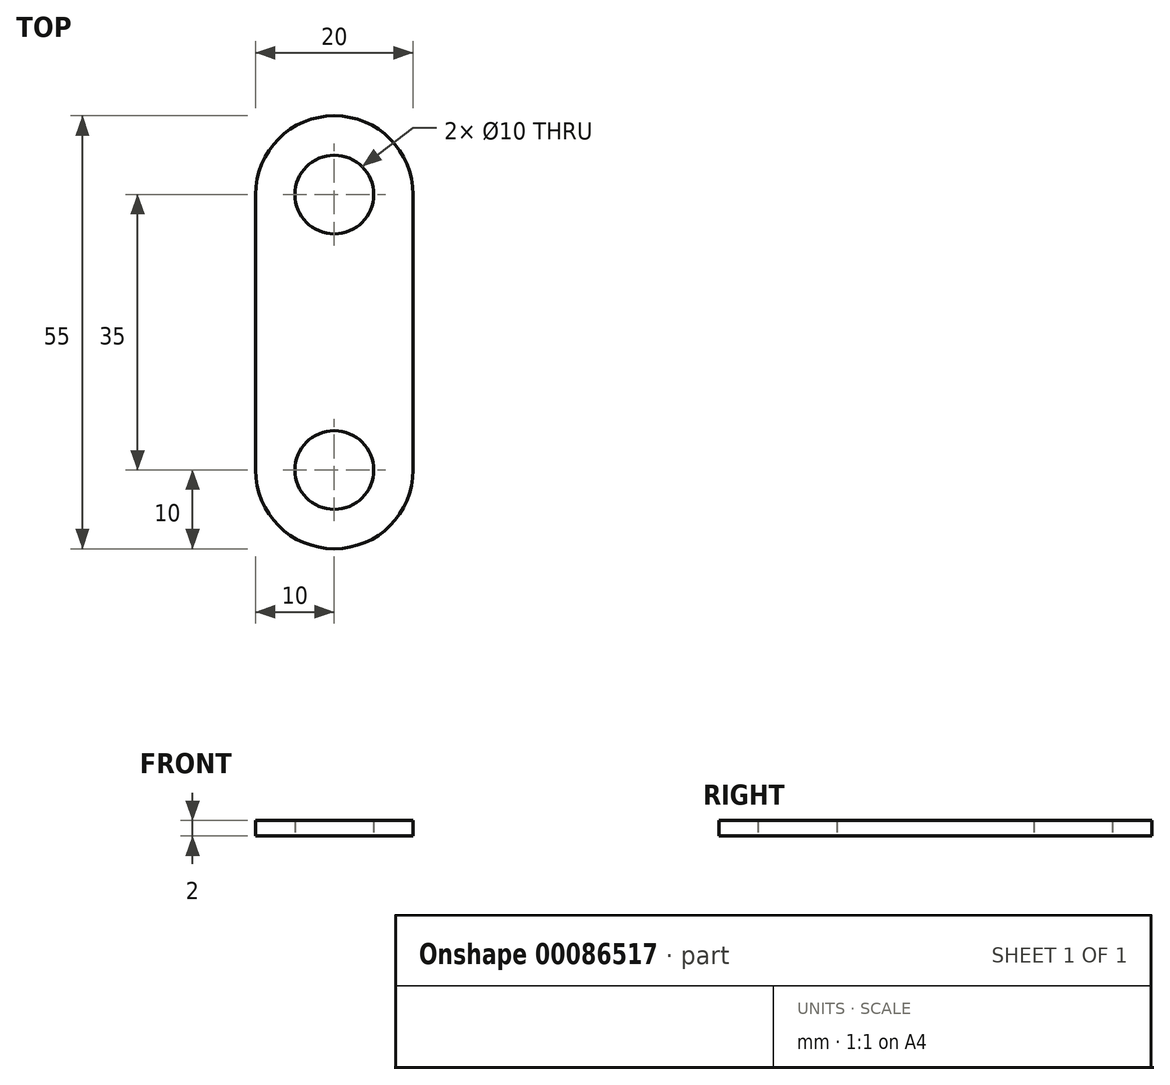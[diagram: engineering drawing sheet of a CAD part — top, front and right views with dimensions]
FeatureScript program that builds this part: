
annotation { "Feature Type Name" : "Feature", "Feature Type Description" : "" }
export const myFeature = defineFeature(function(context is Context, id is Id, definition is map)
    precondition{}
    {
        {
            var Q0;
            Q0=qCreatedBy(makeId("Top.planeOp"),FACE);
            var sketch = newSketch(context, id + "F0", { "sketchPlane" : qUnion([Q0])});
            skLineSegment(sketch, "E0", {"start": v(-10, 17.5) * mm, "end": v(-10, -17.5) * mm});
            skLineSegment(sketch, "E1", {"start": v(10, 17.5) * mm, "end": v(10, -17.5) * mm});
            skArc(sketch, "E2.filletArc", {"start": v(-10, -17.5) * mm, "mid": v(0, -27.5) * mm, "end": v(10, -17.5) * mm});
            skArc(sketch, "E3", {"start": v(-10, 17.5) * mm, "mid": v(0, 27.5) * mm, "end": v(10, 17.5) * mm});
            skLineSegment(sketch, "E4", {"start": v(0, 17.5) * mm, "end": v(0, -17.5) * mm, "construction": true});
            skCircle(sketch, "E5", {"center": v(0, 17.5) * mm, "radius": 5 * mm});
            skCircle(sketch, "E6", {"center": v(0, -17.5) * mm, "radius": 5 * mm});
            skSolve(sketch);
        }
        {
            var Q0;
            Q0=makeQuery(id+"F0.imprint","IMPRINT",FACE,{"disambiguationData":[TD([[makeQuery(id+"F0.imprint","IMPRINT",EDGE,{"derivedFrom":sQuery(id+"F0.wireOp",EDGE,"E0")}),1.0]])]});
            extrude(context, id + "F1", {"entities" : qUnion([Q0]), "depth" : 2 * mm});
        }
    });
